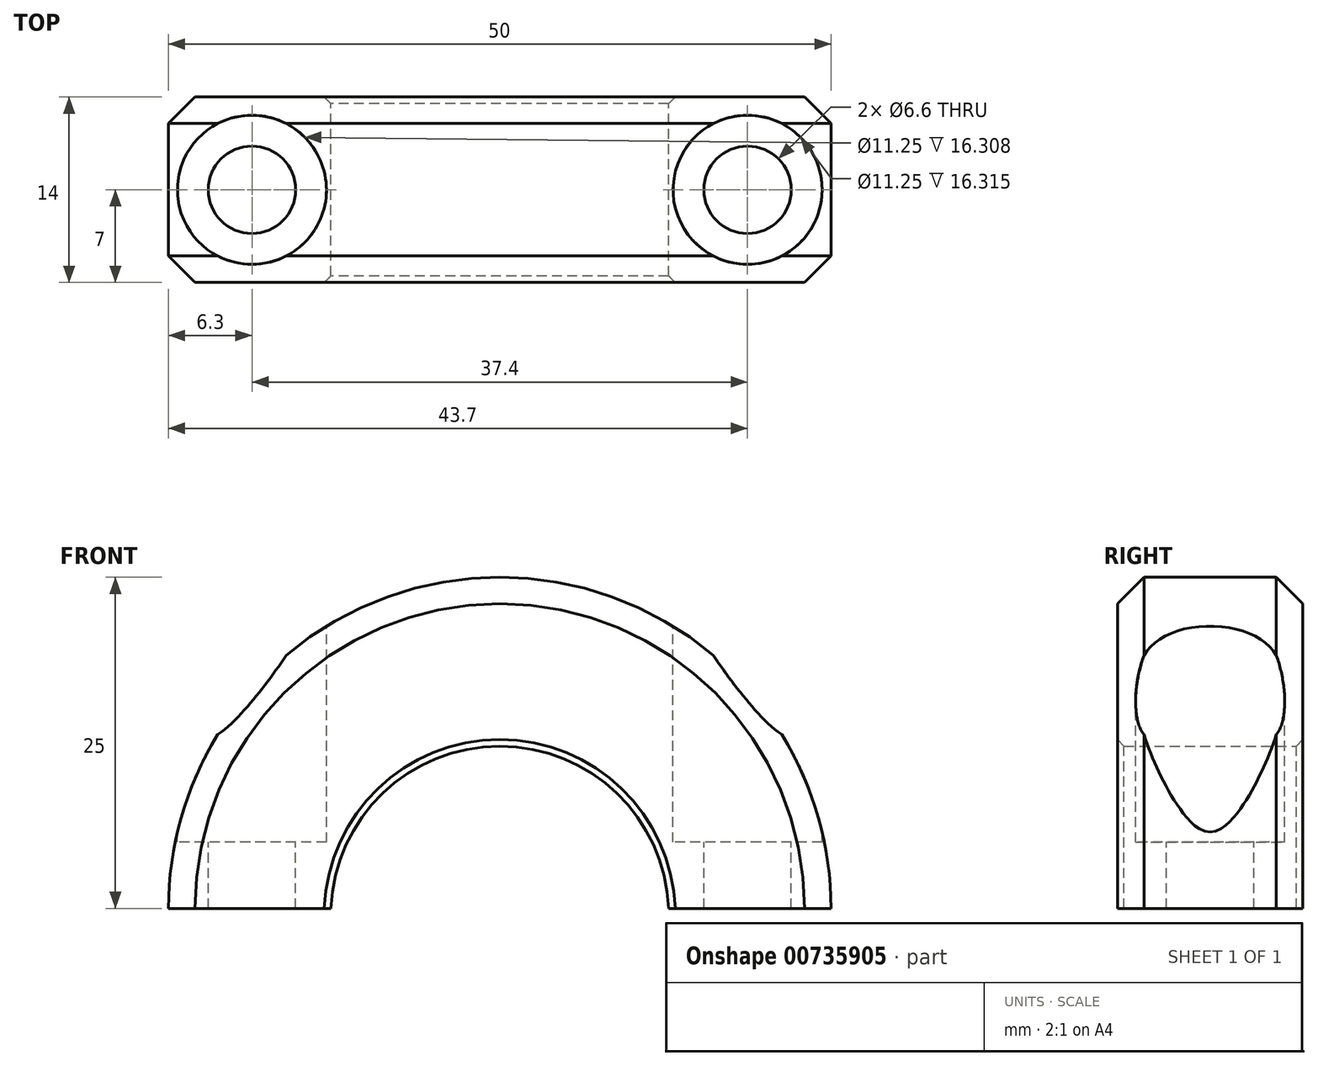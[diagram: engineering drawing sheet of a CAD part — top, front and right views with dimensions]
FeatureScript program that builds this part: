
annotation { "Feature Type Name" : "Feature", "Feature Type Description" : "" }
export const myFeature = defineFeature(function(context is Context, id is Id, definition is map)
    precondition{}
    {
        {
            var Q0;
            Q0=qCreatedBy(makeId("Front.planeOp"),FACE);
            var sketch = newSketch(context, id + "F0", { "sketchPlane" : qUnion([Q0])});
            skArc(sketch, "E0", {"start": v(25, 0) * mm, "mid": v(0, 25) * mm, "end": v(-25, 0) * mm});
            skArc(sketch, "E1", {"start": v(12.74, 0) * mm, "mid": v(0, 12.25) * mm, "end": v(-12.74, 0) * mm});
            skLineSegment(sketch, "E2", {"start": v(12.74, 0) * mm, "end": v(25, 0) * mm});
            skLineSegment(sketch, "E3", {"start": v(-12.74, 0) * mm, "end": v(-25, 0) * mm});
            skSolve(sketch);
        }
        {
            var Q0;
            Q0 = qSketchRegion(id + "F0", true);
            extrude(context, id + "F1", {"entities" : qUnion([Q0]), "depth" : 14 * mm, "offsetDistance" : 25 * mm});
        }
        {
            var Q0;
            Q0=qCreatedBy(makeId("Top.planeOp"),FACE);
            cPlane(context, id + "F2", {"entities" : qUnion([Q0]), "cplaneType" : CPlaneType.OFFSET, "offset" : 25 * mm, "width" : 150 * mm, "height" : 150 * mm});
        }
        {
            var Q0;
            Q0=qCreatedBy(id+"F2.planeOp",FACE);
            var sketch = newSketch(context, id + "F3", { "sketchPlane" : qUnion([Q0])});
            skPoint(sketch, "E4", {"position": v(-18.7, -7) * mm});
            skPoint(sketch, "E5", {"position": v(18.7, -7) * mm});
            skSolve(sketch);
        }
        {
            var Q0;
            Q0=sQuery(id+"F3.wireOp",VERTEX,"E4");
            var Q1;
            Q1=sQuery(id+"F3.wireOp",VERTEX,"E5");
            var Q2;
            Q2=makeQuery(id+"F1.opExtrude","SWEPT_BODY",BODY,{"disambiguationData":[OSD([sQuery(id+"F0.wireOp",EDGE,"E0"),sQuery(id+"F0.wireOp",EDGE,"E1"),sQuery(id+"F0.wireOp",EDGE,"E2"),sQuery(id+"F0.wireOp",EDGE,"E3")])]});
            hole(context, id + "F4", {"style" : HoleStyle.C_BORE, "endStyle" : HoleEndStyle.BLIND, "holeDiameter" : 6.6 * mm, "cBoreDiameter" : 11.25 * mm, "cBoreDepth" : 20 * mm, "majorDiameter" : 5 * mm, "holeDepth" : 30 * mm, "tappedDepth" : 20 * mm, "tapClearance" : 3, "startFromSketch" : true, "locations" : qUnion([Q0, Q1]), "scope" : qUnion([Q2])});
        }
        {
            var Q0;
            Q0=makeQuery(id+"F1.opExtrude","CAP_EDGE",EDGE,{"disambiguationData":[OSD([sQuery(id+"F0.wireOp",EDGE,"E0")])],"isStart":false});
            var Q1;
            Q1=makeQuery(id+"F1.opExtrude","CAP_EDGE",EDGE,{"disambiguationData":[OSD([sQuery(id+"F0.wireOp",EDGE,"E0")])],"isStart":true});
            chamfer(context, id + "F5", {"entities" : qUnion([Q0, Q1]), "width" : 2 * mm, "tangentPropagation" : true});
        }
        {
            var Q0;
            Q0=makeQuery(id+"F1.opExtrude","CAP_EDGE",EDGE,{"disambiguationData":[OSD([sQuery(id+"F0.wireOp",EDGE,"E1")])],"isStart":false});
            var Q1;
            Q1=makeQuery(id+"F1.opExtrude","CAP_EDGE",EDGE,{"disambiguationData":[OSD([sQuery(id+"F0.wireOp",EDGE,"E1")])],"isStart":true});
            chamfer(context, id + "F6", {"entities" : qUnion([Q0, Q1]), "width" : 0.5 * mm, "tangentPropagation" : true});
        }
    });
